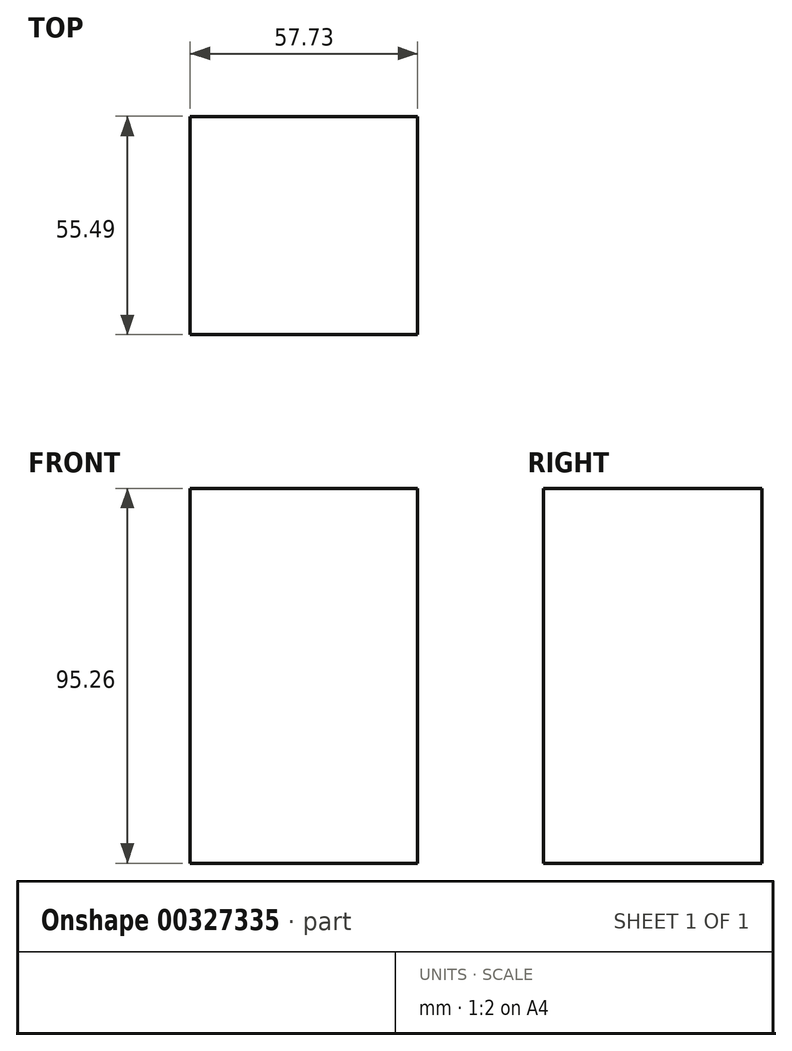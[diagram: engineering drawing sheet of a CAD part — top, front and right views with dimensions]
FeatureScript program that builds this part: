
annotation { "Feature Type Name" : "Feature", "Feature Type Description" : "" }
export const myFeature = defineFeature(function(context is Context, id is Id, definition is map)
    precondition{}
    {
        {
            var Q0;
            Q0=qCreatedBy(makeId("Top.planeOp"),FACE);
            var sketch = newSketch(context, id + "F0", { "sketchPlane" : qUnion([Q0])});
            skLineSegment(sketch, "E0.bottom", {"start": v(0, 0) * mm, "end": v(57.73, 0) * mm});
            skLineSegment(sketch, "E0.top", {"start": v(0, 55.49) * mm, "end": v(57.73, 55.49) * mm});
            skLineSegment(sketch, "E0.left", {"start": v(0, 0) * mm, "end": v(0, 55.49) * mm});
            skLineSegment(sketch, "E0.right", {"start": v(57.73, 0) * mm, "end": v(57.73, 55.49) * mm});
            skSolve(sketch);
        }
        {
            var Q0;
            Q0=makeQuery(id+"F0.imprint","IMPRINT",FACE,{"disambiguationData":[TD([[makeQuery(id+"F0.imprint","IMPRINT",EDGE,{"derivedFrom":sQuery(id+"F0.wireOp",EDGE,"E0.bottom")}),1.0]])]});
            extrude(context, id + "F1", {"entities" : qUnion([Q0]), "oppositeDirection" : true, "depth" : 95.26 * mm});
        }
    });
